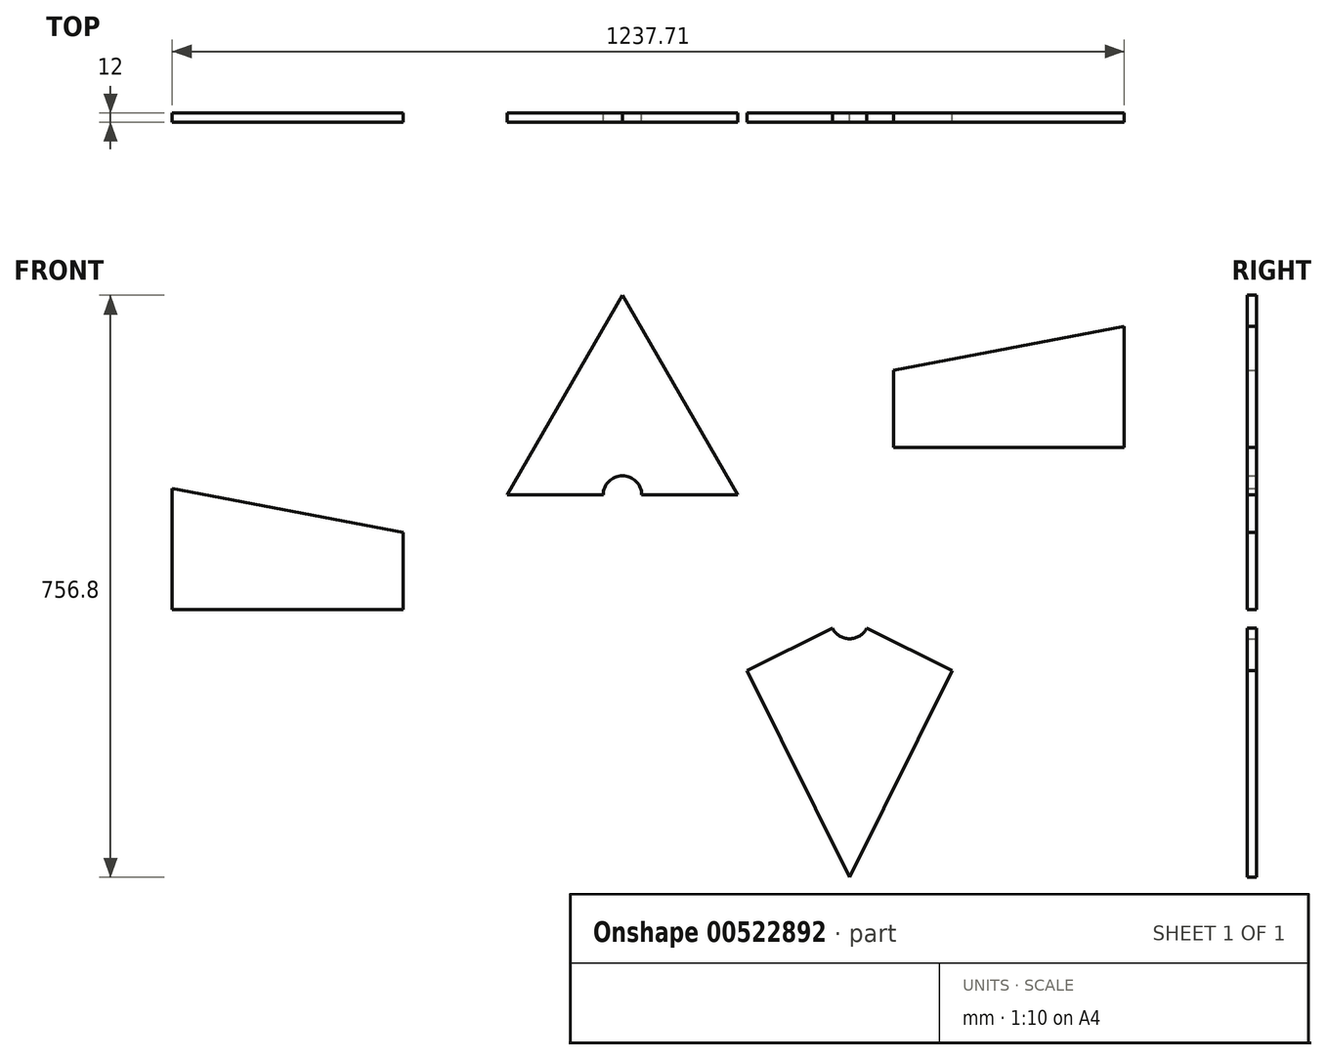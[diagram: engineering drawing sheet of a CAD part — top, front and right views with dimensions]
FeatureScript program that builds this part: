
annotation { "Feature Type Name" : "Feature", "Feature Type Description" : "" }
export const myFeature = defineFeature(function(context is Context, id is Id, definition is map)
    precondition{}
    {
        {
            var Q0;
            Q0=qCreatedBy(makeId("Front.planeOp"),FACE);
            var sketch = newSketch(context, id + "F0", { "sketchPlane" : qUnion([Q0])});
            skLineSegment(sketch, "E0", {"start": v(-96.83, -162.13) * mm, "end": v(203.17, -162.13) * mm});
            skLineSegment(sketch, "E1", {"start": v(203.17, -162.13) * mm, "end": v(53.17, 97.68) * mm});
            skLineSegment(sketch, "E2", {"start": v(53.17, 97.68) * mm, "end": v(-96.83, -162.13) * mm});
            skLineSegment(sketch, "E3", {"start": v(405.53, 0) * mm, "end": v(405.53, -100) * mm});
            skLineSegment(sketch, "E4", {"start": v(405.53, -100) * mm, "end": v(705.53, -100) * mm});
            skLineSegment(sketch, "E5", {"start": v(705.53, -100) * mm, "end": v(705.53, 57) * mm});
            skLineSegment(sketch, "E6", {"start": v(705.53, 57) * mm, "end": v(405.53, 0) * mm});
            skLineSegment(sketch, "E7", {"start": v(-532.18, -310.93) * mm, "end": v(-532.18, -153.93) * mm});
            skLineSegment(sketch, "E8", {"start": v(-532.18, -310.93) * mm, "end": v(-232.18, -310.93) * mm});
            skLineSegment(sketch, "E9", {"start": v(-232.18, -310.93) * mm, "end": v(-232.18, -210.93) * mm});
            skLineSegment(sketch, "E10", {"start": v(-232.18, -210.93) * mm, "end": v(-532.18, -153.93) * mm});
            skLineSegment(sketch, "E11", {"start": v(348.35, -659.12) * mm, "end": v(214.85, -390.47) * mm});
            skLineSegment(sketch, "E12", {"start": v(214.85, -390.47) * mm, "end": v(348.35, -324.12) * mm});
            skLineSegment(sketch, "E13", {"start": v(348.35, -659.12) * mm, "end": v(481.86, -390.47) * mm});
            skLineSegment(sketch, "E14", {"start": v(481.86, -390.47) * mm, "end": v(348.35, -324.12) * mm});
            skCircle(sketch, "E15", {"center": v(53.17, -162.13) * mm, "radius": 25 * mm});
            skCircle(sketch, "E16", {"center": v(348.35, -324.12) * mm, "radius": 25 * mm});
            skSolve(sketch);
        }
        {
            var Q0;
            Q0=makeQuery(id+"F0.imprint","IMPRINT",FACE,{"disambiguationData":[TD([[makeQuery(id+"F0.imprint","IMPRINT",EDGE,{"derivedFrom":sQuery(id+"F0.wireOp",EDGE,"E11")}),-1.0]])]});
            var Q1;
            Q1=makeQuery(id+"F0.imprint","IMPRINT",FACE,{"disambiguationData":[TD([[makeQuery(id+"F0.imprint","IMPRINT",EDGE,{"derivedFrom":sQuery(id+"F0.wireOp",EDGE,"E0")}),1.0]])]});
            var Q2;
            Q2=makeQuery(id+"F0.imprint","IMPRINT",FACE,{"disambiguationData":[TD([[makeQuery(id+"F0.imprint","IMPRINT",EDGE,{"derivedFrom":sQuery(id+"F0.wireOp",EDGE,"E3")}),1.0]])]});
            var Q3;
            Q3=makeQuery(id+"F0.imprint","IMPRINT",FACE,{"disambiguationData":[TD([[makeQuery(id+"F0.imprint","IMPRINT",EDGE,{"derivedFrom":sQuery(id+"F0.wireOp",EDGE,"E7")}),-1.0]])]});
            extrude(context, id + "F1", {"entities" : qUnion([Q0, Q1, Q2, Q3]), "depth" : 12 * mm});
        }
    });
